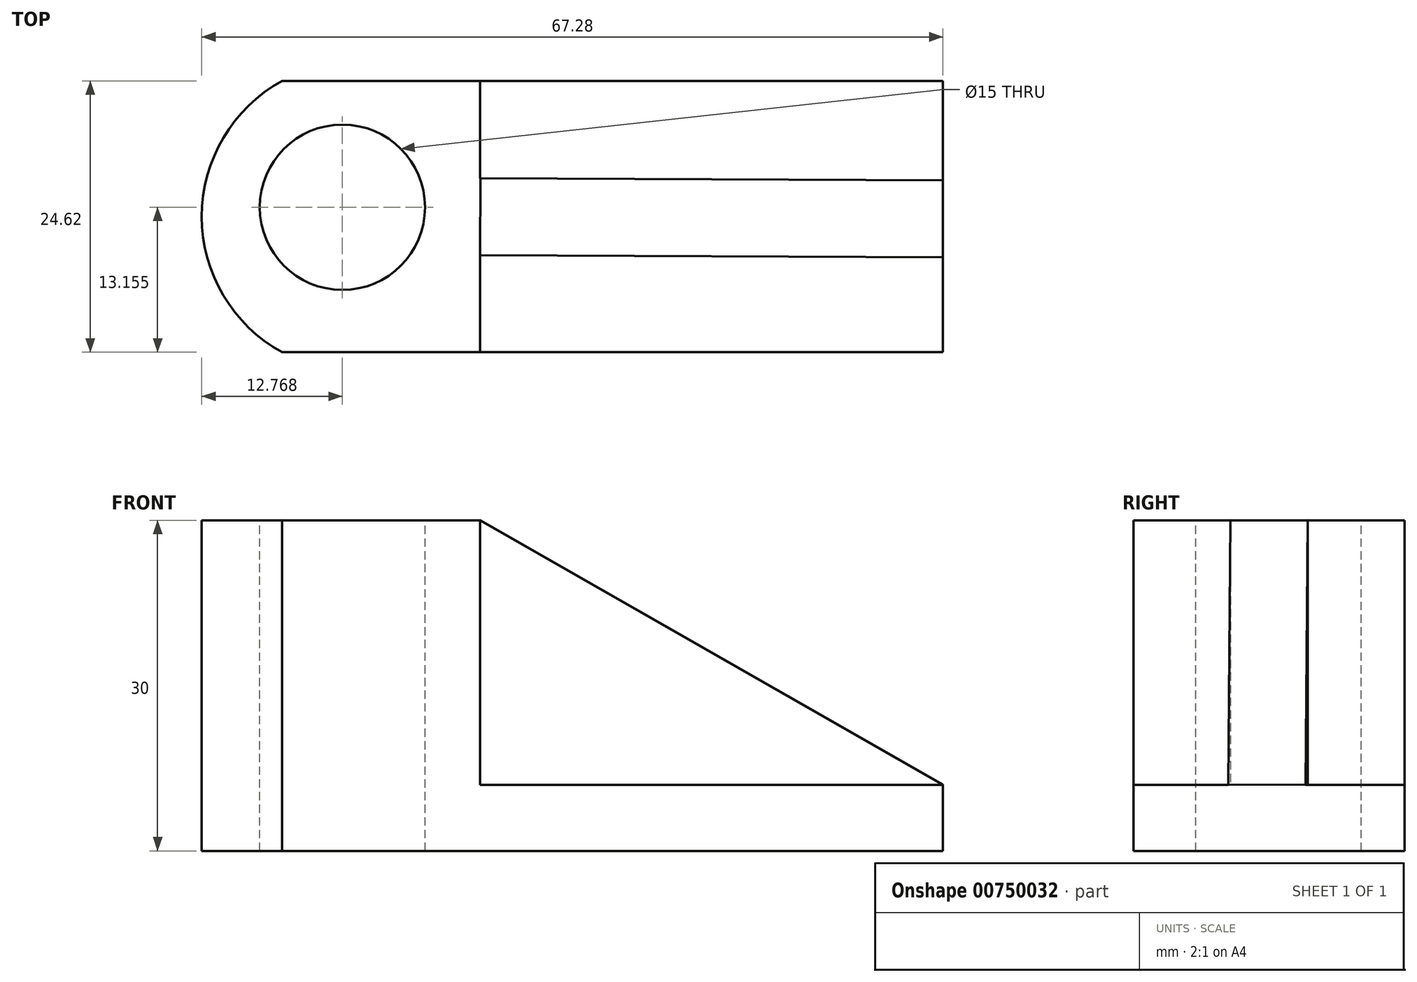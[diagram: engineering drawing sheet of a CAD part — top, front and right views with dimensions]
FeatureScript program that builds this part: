
annotation { "Feature Type Name" : "Feature", "Feature Type Description" : "" }
export const myFeature = defineFeature(function(context is Context, id is Id, definition is map)
    precondition{}
    {
        {
            var Q0;
            Q0=qCreatedBy(makeId("Top.planeOp"),FACE);
            var sketch = newSketch(context, id + "F0", { "sketchPlane" : qUnion([Q0])});
            skLineSegment(sketch, "E0", {"start": v(-30.78, 24.62) * mm, "end": v(-12.78, 24.62) * mm});
            skLineSegment(sketch, "E1", {"start": v(-30.78, 0) * mm, "end": v(-10.7, 0) * mm});
            skArc(sketch, "E2", {"start": v(-30.78, 24.62) * mm, "mid": v(-38.06, 12.3) * mm, "end": v(-30.78, 0) * mm});
            skLineSegment(sketch, "E3", {"start": v(-12.78, 24.62) * mm, "end": v(-12.78, 0) * mm});
            skSolve(sketch);
        }
        {
            var Q0;
            Q0 = qSketchRegion(id + "F0", true);
            extrude(context, id + "F1", {"entities" : qUnion([Q0]), "depth" : 30 * mm, "offsetDistance" : 25.4 * mm});
        }
        {
            var Q0;
            Q0=makeQuery(id+"F1.opExtrude","SWEPT_FACE",FACE,{"disambiguationData":[OSD([sQuery(id+"F0.wireOp",EDGE,"E3")])]});
            var sketch = newSketch(context, id + "F2", { "sketchPlane" : qUnion([Q0])});
            skLineSegment(sketch, "E4.bottom", {"start": v(0, 0) * mm, "end": v(24.62, 0) * mm});
            skLineSegment(sketch, "E4.top", {"start": v(0, 6) * mm, "end": v(24.62, 6) * mm});
            skLineSegment(sketch, "E4.left", {"start": v(0, 0) * mm, "end": v(0, 6) * mm});
            skLineSegment(sketch, "E4.right", {"start": v(24.62, 0) * mm, "end": v(24.62, 6) * mm});
            skSolve(sketch);
        }
        {
            var Q0;
            Q0 = qSketchRegion(id + "F2", true);
            extrude(context, id + "F3", {"entities" : qUnion([Q0]), "operationType" : NewBodyOperationType.ADD, "depth" : 42 * mm, "offsetDistance" : 25 * mm});
        }
        {
            var Q0;
            Q0=makeQuery(id+"F3.opExtrude","SWEPT_FACE",FACE,{"disambiguationData":[OSD([sQuery(id+"F2.wireOp",EDGE,"E4.top")])]});
            var sketch = newSketch(context, id + "F4", { "sketchPlane" : qUnion([Q0])});
            skLineSegment(sketch, "E5", {"start": v(-12.78, 15.8) * mm, "end": v(29.22, 15.62) * mm});
            skLineSegment(sketch, "E6", {"start": v(-12.78, 15.8) * mm, "end": v(-12.78, 8.8) * mm});
            skLineSegment(sketch, "E7", {"start": v(-12.78, 8.8) * mm, "end": v(29.22, 8.62) * mm});
            skLineSegment(sketch, "E8", {"start": v(29.22, 8.62) * mm, "end": v(29.22, 15.62) * mm});
            skSolve(sketch);
        }
        {
            var Q0;
            Q0 = qSketchRegion(id + "F4", true);
            extrude(context, id + "F5", {"entities" : qUnion([Q0]), "operationType" : NewBodyOperationType.ADD, "depth" : 24 * mm, "offsetDistance" : 25 * mm});
        }
        {
            var Q0;
            Q0=makeQuery(id+"F5.opExtrude","SWEPT_FACE",FACE,{"disambiguationData":[OSD([sQuery(id+"F4.wireOp",EDGE,"E7")])]});
            var sketch = newSketch(context, id + "F6", { "sketchPlane" : qUnion([Q0])});
            skLineSegment(sketch, "E9", {"start": v(-12.82, 30) * mm, "end": v(29.18, 6) * mm});
            skLineSegment(sketch, "E10", {"start": v(29.18, 6) * mm, "end": v(29.18, 30) * mm});
            skLineSegment(sketch, "E11", {"start": v(29.18, 30) * mm, "end": v(-12.82, 30) * mm});
            skSolve(sketch);
        }
        {
            var Q0;
            Q0 = qSketchRegion(id + "F6", true);
            extrude(context, id + "F7", {"entities" : qUnion([Q0]), "operationType" : NewBodyOperationType.REMOVE, "oppositeDirection" : true, "depth" : 100 * mm, "offsetDistance" : 25 * mm});
        }
        {
            var Q0;
            Q0=makeQuery(id+"F5.boolean.opBoolean","MERGE",FACE,{"derivedFrom":[makeQuery(id+"F1.opExtrude","CAP_FACE",FACE,{"disambiguationData":[OSD([sQuery(id+"F0.wireOp",EDGE,"E0"),sQuery(id+"F0.wireOp",EDGE,"E1"),sQuery(id+"F0.wireOp",EDGE,"E2"),sQuery(id+"F0.wireOp",EDGE,"E3")])],"isStart":false}),makeQuery(id+"F5.opExtrude","CAP_FACE",FACE,{"disambiguationData":[OSD([sQuery(id+"F4.wireOp",EDGE,"E5"),sQuery(id+"F4.wireOp",EDGE,"E6"),sQuery(id+"F4.wireOp",EDGE,"E7"),sQuery(id+"F4.wireOp",EDGE,"E8")])],"isStart":false})]});
            var sketch = newSketch(context, id + "F8", { "sketchPlane" : qUnion([Q0])});
            skCircle(sketch, "E12", {"center": v(-25.3, 13.16) * mm, "radius": 7.5 * mm});
            skSolve(sketch);
        }
        {
            var Q0;
            Q0 = qSketchRegion(id + "F8", true);
            extrude(context, id + "F9", {"entities" : qUnion([Q0]), "operationType" : NewBodyOperationType.REMOVE, "oppositeDirection" : true, "depth" : 100 * mm, "offsetDistance" : 25 * mm});
        }
    });
